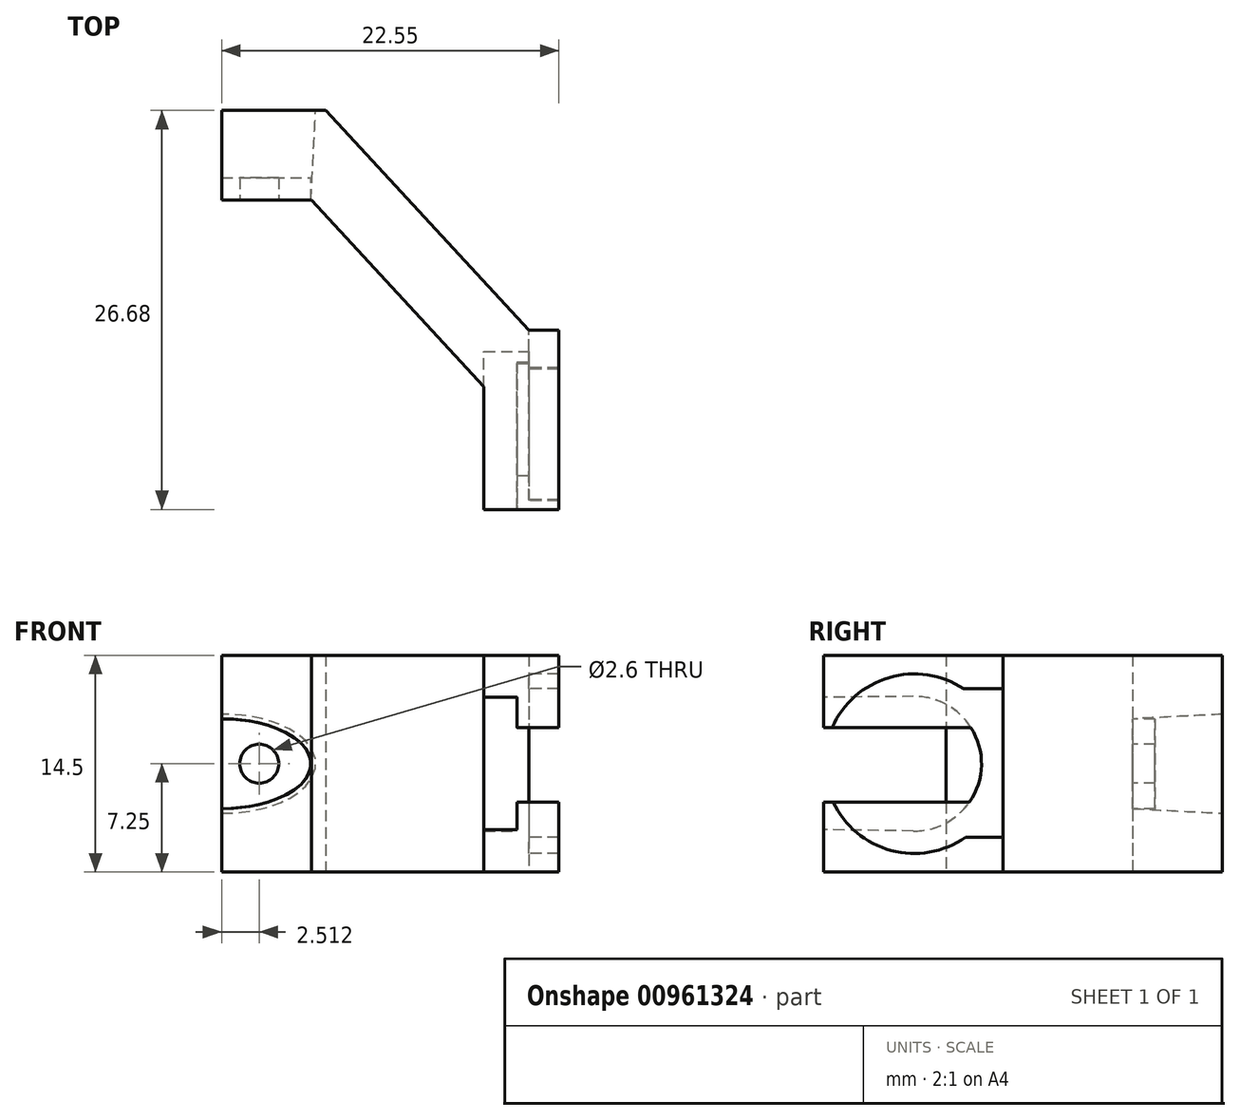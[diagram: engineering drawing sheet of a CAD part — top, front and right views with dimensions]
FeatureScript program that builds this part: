
annotation { "Feature Type Name" : "Feature", "Feature Type Description" : "" }
export const myFeature = defineFeature(function(context is Context, id is Id, definition is map)
    precondition{}
    {
        {
            var Q0;
            Q0=qCreatedBy(makeId("Top.planeOp"),FACE);
            var sketch = newSketch(context, id + "F0", { "sketchPlane" : qUnion([Q0])});
            skLineSegment(sketch, "E0", {"start": v(0, -14.68) * mm, "end": v(-13.59, 0) * mm});
            skLineSegment(sketch, "E1", {"start": v(-13.59, 0) * mm, "end": v(-20.55, 0) * mm});
            skLineSegment(sketch, "E2", {"start": v(-20.55, 0) * mm, "end": v(-20.55, -6) * mm});
            skLineSegment(sketch, "E3", {"start": v(-20.55, -6) * mm, "end": v(-14.55, -6) * mm});
            skLineSegment(sketch, "E4", {"start": v(0, -14.68) * mm, "end": v(0, -26.68) * mm});
            skLineSegment(sketch, "E5", {"start": v(0, -26.68) * mm, "end": v(-3, -26.68) * mm});
            skLineSegment(sketch, "E6", {"start": v(-3, -26.68) * mm, "end": v(-3, -18.48) * mm});
            skLineSegment(sketch, "E7", {"start": v(-3, -18.48) * mm, "end": v(-14.55, -6) * mm});
            skLineSegment(sketch, "E8", {"start": v(-20.55, 0) * mm, "end": v(-20.55, 0) * mm});
            skSolve(sketch);
        }
        {
            var Q0;
            Q0=makeQuery(id+"F0.imprint","IMPRINT",FACE,{"disambiguationData":[TD([[makeQuery(id+"F0.imprint","IMPRINT",EDGE,{"derivedFrom":sQuery(id+"F0.wireOp",EDGE,"E0")}),1.0]])]});
            extrude(context, id + "F1", {"entities" : qUnion([Q0]), "depth" : 14.5 * mm, "offsetDistance" : 25.4 * mm});
        }
        {
            var Q0;
            Q0=makeQuery(id+"F1.opExtrude","SWEPT_FACE",FACE,{"disambiguationData":[OSD([sQuery(id+"F0.wireOp",EDGE,"E4")])]});
            var sketch = newSketch(context, id + "F2", { "sketchPlane" : qUnion([Q0])});
            skCircle(sketch, "E9", {"center": v(-20.61, 7.25) * mm, "radius": 4.5 * mm});
            skPoint(sketch, "E10", {"position": v(-14.68, 7.25) * mm});
            skLineSegment(sketch, "E11", {"start": v(-16.82, 9.67) * mm, "end": v(-24.4, 9.67) * mm});
            skCircle(sketch, "E12", {"center": v(-20.61, 7.25) * mm, "radius": 6 * mm});
            skLineSegment(sketch, "E13", {"start": v(-24.3, 4.68) * mm, "end": v(-26.68, 4.68) * mm});
            skLineSegment(sketch, "E14", {"start": v(-24.4, 9.68) * mm, "end": v(-26.68, 9.68) * mm});
            skLineSegment(sketch, "E15", {"start": v(-24.3, 4.68) * mm, "end": v(-16.92, 4.68) * mm});
            skLineSegment(sketch, "E16", {"start": v(-17.3, 12.26) * mm, "end": v(-14.68, 12.26) * mm});
            skLineSegment(sketch, "E17", {"start": v(-20.66, 11.75) * mm, "end": v(-26.68, 11.69) * mm});
            skLineSegment(sketch, "E18", {"start": v(-20.68, 2.75) * mm, "end": v(-26.68, 2.84) * mm});
            skPoint(sketch, "E18.startSnap0", {"position": v(-20.68, 0) * mm});
            skLineSegment(sketch, "E19", {"start": v(-17.19, 2.32) * mm, "end": v(-14.68, 2.32) * mm});
            skSolve(sketch);
        }
        {
            var Q0;
            Q0=makeQuery(id+"F2.imprint","IMPRINT",FACE,{"disambiguationData":[TD([[makeQuery(id+"F2.imprint","IMPRINT",EDGE,{"derivedFrom":sQuery(id+"F2.wireOp",EDGE,"E9")}),1.0]])]});
            var Q1;
            {var subQ0=sQuery(id+"F2.wireOp",EDGE,"E11");Q1=makeQuery(id+"F2.imprint","IMPRINT",FACE,{"disambiguationData":[TD([[makeQuery(id+"F2.imprint","IMPRINT",EDGE,{"derivedFrom":subQ0}),-1.0]])]});}
            var Q2;
            {var subQ0=sQuery(id+"F2.wireOp",EDGE,"E11");var subQ1=sQuery(id+"F2.wireOp",EDGE,"E9");var subQ2=makeQuery(id+"F2.imprint","INTERSECT",VERTEX,{"disambiguationData":[OD(0.0)],"derivedFrom":[subQ1,subQ0]});Q2=makeQuery(id+"F2.imprint","IMPRINT",FACE,{"disambiguationData":[TD([[makeQuery(id+"F2.imprint","IMPRINT",EDGE,{"disambiguationData":[TD([[subQ2,1.0]])],"derivedFrom":subQ1}),1.0]])]});}
            var Q3;
            {var subQ0=sQuery(id+"F2.wireOp",EDGE,"E15");Q3=makeQuery(id+"F2.imprint","IMPRINT",FACE,{"disambiguationData":[TD([[makeQuery(id+"F2.imprint","IMPRINT",EDGE,{"derivedFrom":subQ0}),-1.0]])]});}
            var Q4;
            {var subQ1=sQuery(id+"F2.wireOp",EDGE,"E9");var subQ7=makeQuery(id+"F2.imprint","INTERSECT",VERTEX,{"disambiguationData":[OD(1.0)],"derivedFrom":[subQ1,sQuery(id+"F2.wireOp",EDGE,"E11")]});Q4=makeQuery(id+"F2.imprint","IMPRINT",FACE,{"disambiguationData":[TD([[makeQuery(id+"F2.imprint","IMPRINT",EDGE,{"disambiguationData":[TD([[subQ7,1.0]])],"derivedFrom":subQ1}),-1.0]])]});}
            var Q5;
            {var subQ0=sQuery(id+"F2.wireOp",EDGE,"E14");var subQ1=sQuery(id+"F2.wireOp",EDGE,"E12");var subQ2=makeQuery(id+"F2.imprint","INTERSECT",VERTEX,{"derivedFrom":[subQ1,subQ0]});Q5=makeQuery(id+"F2.imprint","IMPRINT",FACE,{"disambiguationData":[TD([[makeQuery(id+"F2.imprint","IMPRINT",EDGE,{"disambiguationData":[TD([[subQ2,-1.0]])],"derivedFrom":subQ1}),-1.0]])]});}
            var Q6;
            {var subQ0=sQuery(id+"F2.wireOp",EDGE,"E17");var subQ1=sQuery(id+"F2.wireOp",EDGE,"E12");var subQ2=makeQuery(id+"F2.imprint","INTERSECT",VERTEX,{"derivedFrom":[subQ1,subQ0]});Q6=makeQuery(id+"F2.imprint","IMPRINT",FACE,{"disambiguationData":[TD([[makeQuery(id+"F2.imprint","IMPRINT",EDGE,{"disambiguationData":[TD([[subQ2,-1.0]])],"derivedFrom":subQ1}),-1.0]])]});}
            var Q7;
            {var subQ0=sQuery(id+"F2.wireOp",EDGE,"E13");var subQ1=sQuery(id+"F2.wireOp",EDGE,"E12");var subQ2=makeQuery(id+"F2.imprint","INTERSECT",VERTEX,{"derivedFrom":[subQ1,subQ0]});Q7=makeQuery(id+"F2.imprint","IMPRINT",FACE,{"disambiguationData":[TD([[makeQuery(id+"F2.imprint","IMPRINT",EDGE,{"disambiguationData":[TD([[subQ2,-1.0]])],"derivedFrom":subQ1}),-1.0]])]});}
            var Q8;
            {var subQ0=sQuery(id+"F2.wireOp",EDGE,"E14");var subQ1=sQuery(id+"F2.wireOp",EDGE,"E9");var subQ2=makeQuery(id+"F2.imprint","INTERSECT",VERTEX,{"derivedFrom":[subQ1,subQ0]});Q8=makeQuery(id+"F2.imprint","IMPRINT",FACE,{"disambiguationData":[TD([[makeQuery(id+"F2.imprint","IMPRINT",EDGE,{"disambiguationData":[TD([[subQ2,1.0]])],"derivedFrom":subQ1}),-1.0]])]});}
            var Q9;
            {var subQ0=sQuery(id+"F2.wireOp",EDGE,"E13");var subQ5=sQuery(id+"F2.wireOp",EDGE,"E12");var subQ6=makeQuery(id+"F2.imprint","INTERSECT",VERTEX,{"derivedFrom":[subQ5,subQ0]});Q9=makeQuery(id+"F2.imprint","IMPRINT",FACE,{"disambiguationData":[TD([[makeQuery(id+"F2.imprint","IMPRINT",EDGE,{"disambiguationData":[TD([[subQ6,-1.0]])],"derivedFrom":subQ5}),1.0]])]});}
            extrude(context, id + "F3", {"entities" : qUnion([Q0, Q1, Q2, Q3, Q4, Q5, Q6, Q7, Q8, Q9]), "operationType" : NewBodyOperationType.REMOVE, "oppositeDirection" : true, "depth" : 3 * mm, "offsetDistance" : 25.4 * mm});
        }
        {
            var Q0;
            Q0=makeQuery(id+"F1.opExtrude","SWEPT_FACE",FACE,{"disambiguationData":[OSD([sQuery(id+"F0.wireOp",EDGE,"E3")])]});
            var sketch = newSketch(context, id + "F4", { "sketchPlane" : qUnion([Q0])});
            skEllipse(sketch, "E20", {"center": v(-20.55, 7.25) * mm, "majorRadius": 5.97 * mm, "minorRadius": 3 * mm, "majorAxis": v(1, 0)});
            skLineSegment(sketch, "E21", {"start": v(-14.55, 12.5) * mm, "end": v(-20.55, 12.5) * mm});
            skCircle(sketch, "E22", {"center": v(-18.04, 7.25) * mm, "radius": 1.3 * mm});
            skSolve(sketch);
        }
        {
            var Q0;
            {var subQ0=sQuery(id+"F4.wireOp",EDGE,"E20");var subQ1=makeQuery(id+"F1.opExtrude","SWEPT_EDGE",EDGE,{"disambiguationData":[OSD([sQuery(id+"F0.wireOp",EDGE,"E2"),sQuery(id+"F0.wireOp",EDGE,"E3")])]});var subQ2=makeQuery(id+"F4.imprint","INTERSECT",VERTEX,{"disambiguationData":[OD(0.0)],"derivedFrom":[subQ1,subQ0]});Q0=makeQuery(id+"F4.imprint","IMPRINT",FACE,{"disambiguationData":[TD([[makeQuery(id+"F4.imprint","IMPRINT",EDGE,{"disambiguationData":[TD([[subQ2,-1.0]])],"derivedFrom":subQ0}),1.0]])]});}
            var Q1;
            Q1=makeQuery(id+"F4.imprint","IMPRINT",FACE,{"disambiguationData":[TD([[makeQuery(id+"F4.imprint","IMPRINT",EDGE,{"derivedFrom":sQuery(id+"F4.wireOp",EDGE,"E22")}),1.0]])]});
            var Q2;
            Q2=sQuery(id+"F4.wireOp",EDGE,"E20");
            extrude(context, id + "F5", {"entities" : qUnion([Q0, Q1]), "operationType" : NewBodyOperationType.REMOVE, "surfaceOperationType" : NewSurfaceOperationType.ADD, "surfaceEntities" : qUnion([Q2]), "oppositeDirection" : true, "depth" : 6 * mm, "offsetDistance" : 25.4 * mm, "hasDraft" : true, "draftAngle" : 3 * degree});
        }
        {
            var Q0;
            {var subQ0=sQuery(id+"F2.wireOp",EDGE,"E11");Q0=makeQuery(id+"F2.imprint","IMPRINT",FACE,{"disambiguationData":[TD([[makeQuery(id+"F2.imprint","IMPRINT",EDGE,{"derivedFrom":subQ0}),-1.0]])]});}
            var Q1;
            {var subQ0=sQuery(id+"F2.wireOp",EDGE,"E15");Q1=makeQuery(id+"F2.imprint","IMPRINT",FACE,{"disambiguationData":[TD([[makeQuery(id+"F2.imprint","IMPRINT",EDGE,{"derivedFrom":subQ0}),-1.0]])]});}
            var Q2;
            {var subQ0=sQuery(id+"F2.wireOp",EDGE,"E14");var subQ1=sQuery(id+"F2.wireOp",EDGE,"E9");var subQ2=makeQuery(id+"F2.imprint","INTERSECT",VERTEX,{"derivedFrom":[subQ1,subQ0]});Q2=makeQuery(id+"F2.imprint","IMPRINT",FACE,{"disambiguationData":[TD([[makeQuery(id+"F2.imprint","IMPRINT",EDGE,{"disambiguationData":[TD([[subQ2,1.0]])],"derivedFrom":subQ1}),-1.0]])]});}
            var Q3;
            {var subQ0=sQuery(id+"F2.wireOp",EDGE,"E13");var subQ5=sQuery(id+"F2.wireOp",EDGE,"E12");var subQ6=makeQuery(id+"F2.imprint","INTERSECT",VERTEX,{"derivedFrom":[subQ5,subQ0]});Q3=makeQuery(id+"F2.imprint","IMPRINT",FACE,{"disambiguationData":[TD([[makeQuery(id+"F2.imprint","IMPRINT",EDGE,{"disambiguationData":[TD([[subQ6,-1.0]])],"derivedFrom":subQ5}),1.0]])]});}
            var Q4;
            {var subQ0=sQuery(id+"F2.wireOp",EDGE,"E17");var subQ1=sQuery(id+"F2.wireOp",EDGE,"E12");var subQ2=makeQuery(id+"F2.imprint","INTERSECT",VERTEX,{"derivedFrom":[subQ1,subQ0]});Q4=makeQuery(id+"F2.imprint","IMPRINT",FACE,{"disambiguationData":[TD([[makeQuery(id+"F2.imprint","IMPRINT",EDGE,{"disambiguationData":[TD([[subQ2,-1.0]])],"derivedFrom":subQ1}),-1.0]])]});}
            var Q5;
            {var subQ0=sQuery(id+"F2.wireOp",EDGE,"E13");var subQ1=sQuery(id+"F2.wireOp",EDGE,"E12");var subQ2=makeQuery(id+"F2.imprint","INTERSECT",VERTEX,{"derivedFrom":[subQ1,subQ0]});Q5=makeQuery(id+"F2.imprint","IMPRINT",FACE,{"disambiguationData":[TD([[makeQuery(id+"F2.imprint","IMPRINT",EDGE,{"disambiguationData":[TD([[subQ2,-1.0]])],"derivedFrom":subQ1}),-1.0]])]});}
            extrude(context, id + "F6", {"entities" : qUnion([Q0, Q1, Q2, Q3, Q4, Q5]), "operationType" : NewBodyOperationType.ADD, "oppositeDirection" : true, "depth" : 0.8 * mm, "offsetDistance" : 25.4 * mm});
        }
        {
            var Q0;
            {var subQ2=sQuery(id+"F2.wireOp",EDGE,"E16");Q0=makeQuery(id+"F2.imprint","IMPRINT",FACE,{"disambiguationData":[TD([[makeQuery(id+"F2.imprint","IMPRINT",EDGE,{"derivedFrom":subQ2}),1.0]])]});}
            var Q1;
            {var subQ0=sQuery(id+"F2.wireOp",EDGE,"E17");var subQ1=sQuery(id+"F2.wireOp",EDGE,"E12");var subQ2=makeQuery(id+"F2.imprint","INTERSECT",VERTEX,{"derivedFrom":[subQ1,subQ0]});Q1=makeQuery(id+"F2.imprint","IMPRINT",FACE,{"disambiguationData":[TD([[makeQuery(id+"F2.imprint","IMPRINT",EDGE,{"disambiguationData":[TD([[subQ2,-1.0]])],"derivedFrom":subQ1}),-1.0]])]});}
            extrude(context, id + "F7", {"entities" : qUnion([Q0, Q1]), "operationType" : NewBodyOperationType.ADD, "depth" : 2 * mm, "offsetDistance" : 25.4 * mm});
        }
        {
            var Q0;
            {var subQ0=sQuery(id+"F0.wireOp",EDGE,"E5");var subQ1=sQuery(id+"F0.wireOp",EDGE,"E4");var subQ2=makeQuery(id+"F1.opExtrude","SWEPT_EDGE",EDGE,{"disambiguationData":[OSD([subQ1,subQ0])]});var subQ3=sQuery(id+"F2.wireOp",EDGE,"E17");Q0=makeQuery(id+"F7.boolean.opBoolean","MERGE",FACE,{"derivedFrom":[makeQuery(id+"F6.boolean.opBoolean","MERGE",FACE,{"derivedFrom":[makeQuery(id+"F3.boolean.opBoolean","SPLIT",FACE,{"disambiguationData":[TD([makeQuery(id+"F3.opExtrude","SWEPT_FACE",FACE,{"disambiguationData":[OSD([subQ3])]})])],"derivedFrom":makeQuery(id+"F1.opExtrude","SWEPT_FACE",FACE,{"disambiguationData":[OSD([subQ0])]})}),makeQuery(id+"F6.opExtrude","SWEPT_FACE",FACE,{"disambiguationData":[OSD([subQ1,subQ0]),TDD([makeQuery(id+"F2.imprint","IMPRINT",EDGE,{"disambiguationData":[TD([[makeQuery(id+"F2.imprint","INTERSECT",VERTEX,{"derivedFrom":[subQ2,sQuery(id+"F2.wireOp",EDGE,"E14")]}),1.0]])],"derivedFrom":subQ2})])]})]}),makeQuery(id+"F7.opExtrude","SWEPT_FACE",FACE,{"disambiguationData":[OSD([subQ1,subQ0])]})]});}
            var sketch = newSketch(context, id + "F8", { "sketchPlane" : qUnion([Q0])});
            skLineSegment(sketch, "E23", {"start": v(-3, 11.69) * mm, "end": v(-3, 0) * mm});
            skLineSegment(sketch, "E24", {"start": v(-3, 0) * mm, "end": v(0, 0) * mm});
            skLineSegment(sketch, "E25", {"start": v(0, 0) * mm, "end": v(0, 9.68) * mm});
            skLineSegment(sketch, "E26", {"start": v(2, 9.68) * mm, "end": v(2, 0) * mm});
            skLineSegment(sketch, "E27", {"start": v(2, 0) * mm, "end": v(0, 0) * mm});
            skLineSegment(sketch, "E28", {"start": v(-3, 2.85) * mm, "end": v(-1, 2.85) * mm});
            skLineSegment(sketch, "E29", {"start": v(-1, 2.85) * mm, "end": v(-1, 4.67) * mm});
            skLineSegment(sketch, "E30", {"start": v(-1, 4.67) * mm, "end": v(0, 4.67) * mm});
            skLineSegment(sketch, "E31", {"start": v(0, 4.67) * mm, "end": v(2, 4.67) * mm});
            skSolve(sketch);
        }
        {
            var Q0;
            Q0=makeQuery(id+"F4.imprint","IMPRINT",FACE,{"disambiguationData":[TD([[makeQuery(id+"F4.imprint","IMPRINT",EDGE,{"derivedFrom":sQuery(id+"F4.wireOp",EDGE,"E22")}),-1.0]])]});
            extrude(context, id + "F9", {"entities" : qUnion([Q0]), "operationType" : NewBodyOperationType.ADD, "oppositeDirection" : true, "depth" : 1.5 * mm, "offsetDistance" : 25 * mm});
        }
        {
            var Q0;
            {var subQ0=sQuery(id+"F0.wireOp",EDGE,"E4");var subQ1=makeQuery(id+"F1.opExtrude","CAP_EDGE",EDGE,{"disambiguationData":[OSD([subQ0])],"isStart":true});Q0=makeQuery(id+"F2.imprint","IMPRINT",FACE,{"disambiguationData":[TD([[makeQuery(id+"F2.imprint","IMPRINT",EDGE,{"derivedFrom":subQ1}),-1.0]])]});}
            var Q1;
            {var subQ0=sQuery(id+"F2.wireOp",EDGE,"E13");var subQ1=sQuery(id+"F2.wireOp",EDGE,"E12");var subQ2=makeQuery(id+"F2.imprint","INTERSECT",VERTEX,{"derivedFrom":[subQ1,subQ0]});Q1=makeQuery(id+"F2.imprint","IMPRINT",FACE,{"disambiguationData":[TD([[makeQuery(id+"F2.imprint","IMPRINT",EDGE,{"disambiguationData":[TD([[subQ2,-1.0]])],"derivedFrom":subQ1}),-1.0]])]});}
            extrude(context, id + "F10", {"entities" : qUnion([Q0, Q1]), "operationType" : NewBodyOperationType.ADD, "depth" : 2 * mm, "offsetDistance" : 25 * mm});
        }
    });
